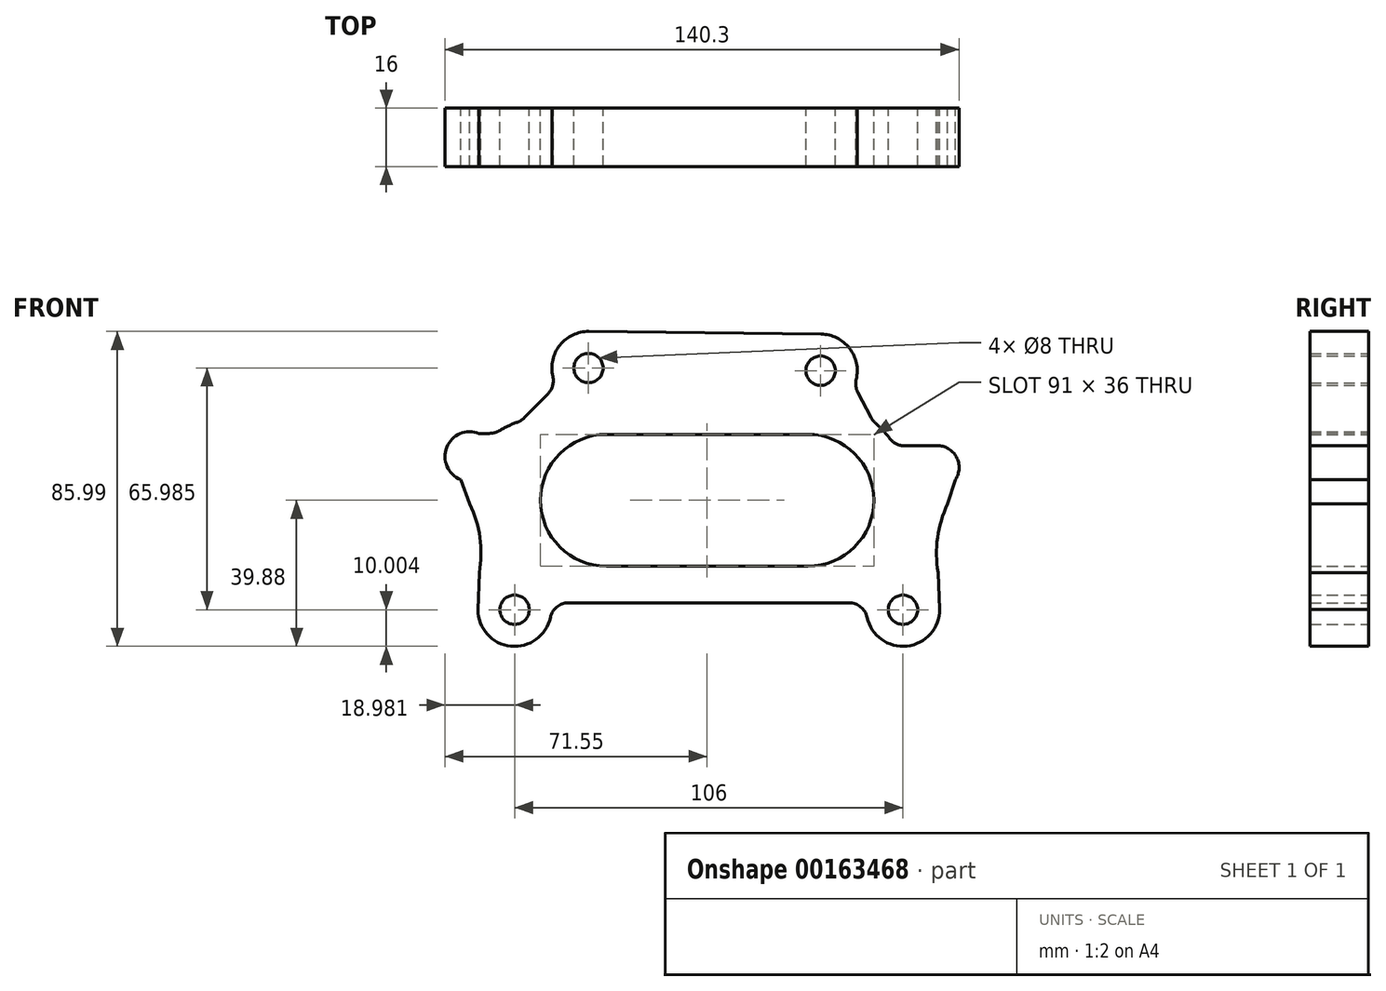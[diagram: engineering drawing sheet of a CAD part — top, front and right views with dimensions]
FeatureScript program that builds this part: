
annotation { "Feature Type Name" : "Feature", "Feature Type Description" : "" }
export const myFeature = defineFeature(function(context is Context, id is Id, definition is map)
    precondition{}
    {
        {
            var Q0;
            Q0=qCreatedBy(makeId("Front.planeOp"),FACE);
            var sketch = newSketch(context, id + "F0", { "sketchPlane" : qUnion([Q0])});
            skLineSegment(sketch, "E0", {"start": v(0, 0) * mm, "end": v(55, 0) * mm, "construction": true});
            skArc(sketch, "E1", {"start": v(0, 18) * mm, "mid": v(-18, 0) * mm, "end": v(0, -18) * mm});
            skArc(sketch, "E2", {"start": v(55, -18) * mm, "mid": v(73, 0) * mm, "end": v(55, 18) * mm});
            skLineSegment(sketch, "E3", {"start": v(0, 18) * mm, "end": v(55, 18) * mm});
            skLineSegment(sketch, "E4", {"start": v(0, -18) * mm, "end": v(55, -18) * mm});
            skLineSegment(sketch, "E5", {"start": v(0, 0) * mm, "end": v(0, -30) * mm, "construction": true});
            skLineSegment(sketch, "E6", {"start": v(0, 0) * mm, "end": v(-25.07, -29.88) * mm, "construction": true});
            skLineSegment(sketch, "E7", {"start": v(0, -30) * mm, "end": v(66, -30) * mm, "construction": true});
            skPoint(sketch, "E8", {"position": v(-25.07, -29.88) * mm});
            skArc(sketch, "E9", {"start": v(-35.04, -29.08) * mm, "mid": v(-26.51, -39.77) * mm, "end": v(-15.29, -31.96) * mm});
            skLineSegment(sketch, "E10", {"start": v(-25.07, -29.88) * mm, "end": v(58.46, 35.38) * mm, "construction": true});
            skPoint(sketch, "E11", {"position": v(58.46, 35.38) * mm});
            skArc(sketch, "E12", {"start": v(68.18, 33.04) * mm, "mid": v(66.35, 41.53) * mm, "end": v(58.57, 45.38) * mm});
            skLineSegment(sketch, "E13", {"start": v(-25.07, -29.88) * mm, "end": v(-4.9, 36.1) * mm, "construction": true});
            skPoint(sketch, "E14", {"position": v(-4.9, 36.1) * mm});
            skArc(sketch, "E15", {"start": v(-4.78, 46.1) * mm, "mid": v(-12.7, 42.36) * mm, "end": v(-14.63, 33.81) * mm});
            skLineSegment(sketch, "E16", {"start": v(-25.07, -29.88) * mm, "end": v(80.93, -29.88) * mm, "construction": true});
            skPoint(sketch, "E17", {"position": v(80.93, -29.88) * mm});
            skArc(sketch, "E18", {"start": v(71.15, -31.96) * mm, "mid": v(82.31, -39.78) * mm, "end": v(90.9, -29.2) * mm});
            skLineSegment(sketch, "E19", {"start": v(-25.07, -29.88) * mm, "end": v(-34.75, 8.94) * mm, "construction": true});
            skLineSegment(sketch, "E20", {"start": v(-34.75, 8.94) * mm, "end": v(90.25, 8.94) * mm, "construction": true});
            skArc(sketch, "E21", {"start": v(95.28, 5.66) * mm, "mid": v(95.52, 11.82) * mm, "end": v(90.2, 14.94) * mm});
            skLineSegment(sketch, "E22", {"start": v(-25.07, -29.88) * mm, "end": v(-65.21, -14.47) * mm, "construction": true});
            skArc(sketch, "E23", {"start": v(-34.67, -19.75) * mm, "mid": v(-34.51, -10.18) * mm, "end": v(-37.28, -1.01) * mm});
            skLineSegment(sketch, "E24", {"start": v(80.93, -29.88) * mm, "end": v(121.08, -14.47) * mm, "construction": true});
            skArc(sketch, "E25", {"start": v(93.15, -1.01) * mm, "mid": v(90.37, -10.18) * mm, "end": v(90.53, -19.75) * mm});
            skLineSegment(sketch, "E26", {"start": v(68.61, 29.55) * mm, "end": v(72.28, 22.53) * mm});
            skLineSegment(sketch, "E27", {"start": v(81.42, 14.85) * mm, "end": v(90.2, 14.94) * mm});
            skLineSegment(sketch, "E28", {"start": v(95.28, 5.66) * mm, "end": v(93.15, -1.01) * mm});
            skLineSegment(sketch, "E29", {"start": v(90.93, -29.74) * mm, "end": v(90.53, -19.75) * mm});
            skLineSegment(sketch, "E30", {"start": v(27.5, 18) * mm, "end": v(27.5, 28) * mm, "construction": true});
            skLineSegment(sketch, "E31", {"start": v(-34.75, 18.27) * mm, "end": v(-31.85, 18.27) * mm});
            skLineSegment(sketch, "E32", {"start": v(-15.92, 29.17) * mm, "end": v(-22.42, 22.53) * mm});
            skLineSegment(sketch, "E33", {"start": v(-39.77, 5.66) * mm, "end": v(-37.28, -1.01) * mm});
            skLineSegment(sketch, "E34", {"start": v(-34.67, -19.75) * mm, "end": v(-35.07, -29.88) * mm});
            skLineSegment(sketch, "E35", {"start": v(27.5, -18) * mm, "end": v(27.5, -28) * mm, "construction": true});
            skLineSegment(sketch, "E36", {"start": v(27.5, -28) * mm, "end": v(-10.4, -28) * mm});
            skLineSegment(sketch, "E37", {"start": v(27.5, -28) * mm, "end": v(66.26, -28) * mm});
            skArc(sketch, "E38.trimOffspring", {"start": v(-24.32, 21.31) * mm, "mid": v(-26.86, 20.27) * mm, "end": v(-29.28, 18.98) * mm});
            skArc(sketch, "E39.trimOffspring", {"start": v(-34.75, 18.27) * mm, "mid": v(-43.56, 14.47) * mm, "end": v(-39.77, 5.66) * mm});
            skArc(sketch, "E40.trimOffspring", {"start": v(77.37, 16.84) * mm, "mid": v(75.5, 19.06) * mm, "end": v(73.42, 21.08) * mm});
            skPoint(sketch, "E41.visualSharp", {"position": v(0.96, 28) * mm});
            skPoint(sketch, "E42.visualSharp", {"position": v(51.72, 28) * mm});
            skPoint(sketch, "E43.visualSharp", {"position": v(-15.25, -28) * mm});
            skArc(sketch, "E43.filletArc", {"start": v(-10.4, -28) * mm, "mid": v(-13.54, -29.11) * mm, "end": v(-15.29, -31.96) * mm});
            skPoint(sketch, "E44.visualSharp", {"position": v(71.1, -28) * mm});
            skArc(sketch, "E44.filletArc", {"start": v(71.15, -31.96) * mm, "mid": v(69.4, -29.11) * mm, "end": v(66.26, -28) * mm});
            skPoint(sketch, "E45.visualSharp", {"position": v(67.64, 31.41) * mm});
            skArc(sketch, "E45.filletArc", {"start": v(68.18, 33.04) * mm, "mid": v(68.08, 31.26) * mm, "end": v(68.61, 29.55) * mm});
            skPoint(sketch, "E46.visualSharp", {"position": v(72.74, 21.67) * mm});
            skArc(sketch, "E46.filletArc", {"start": v(72.28, 22.53) * mm, "mid": v(72.79, 21.76) * mm, "end": v(73.42, 21.08) * mm});
            skPoint(sketch, "E47.visualSharp", {"position": v(78.76, 14.82) * mm});
            skArc(sketch, "E47.filletArc", {"start": v(77.37, 16.84) * mm, "mid": v(79.16, 15.36) * mm, "end": v(81.42, 14.85) * mm});
            skPoint(sketch, "E48.visualSharp", {"position": v(-30.4, 18.27) * mm});
            skArc(sketch, "E48.filletArc", {"start": v(-31.85, 18.27) * mm, "mid": v(-30.52, 18.45) * mm, "end": v(-29.28, 18.98) * mm});
            skPoint(sketch, "E49.visualSharp", {"position": v(-23.26, 21.67) * mm});
            skArc(sketch, "E49.filletArc", {"start": v(-24.32, 21.31) * mm, "mid": v(-23.3, 21.81) * mm, "end": v(-22.42, 22.53) * mm});
            skPoint(sketch, "E50.visualSharp", {"position": v(-13.72, 31.41) * mm});
            skArc(sketch, "E50.filletArc", {"start": v(-15.92, 29.17) * mm, "mid": v(-14.68, 31.32) * mm, "end": v(-14.63, 33.81) * mm});
            skLineSegment(sketch, "E51", {"start": v(-4.78, 46.1) * mm, "end": v(58.85, 45.38) * mm});
            skPoint(sketch, "E51.startSnap0", {"position": v(-5, 46.1) * mm});
            skPoint(sketch, "E51.endSnap0", {"position": v(58.85, 45.38) * mm});
            skSolve(sketch);
        }
        {
            var Q0;
            Q0=makeQuery(id+"F0.imprint","IMPRINT",FACE,{"disambiguationData":[TD([[makeQuery(id+"F0.imprint","IMPRINT",EDGE,{"derivedFrom":sQuery(id+"F0.wireOp",EDGE,"E1")}),-1.0]])]});
            extrude(context, id + "F1", {"entities" : qUnion([Q0]), "depth" : 16 * mm});
        }
        {
            var Q0;
            Q0=sQuery(id+"F0.wireOp",VERTEX,"E11");
            var Q1;
            Q1=sQuery(id+"F0.wireOp",VERTEX,"E14");
            var Q2;
            Q2=sQuery(id+"F0.wireOp",VERTEX,"E8");
            var Q3;
            Q3=sQuery(id+"F0.wireOp",VERTEX,"E17");
            var Q4;
            Q4=makeQuery(id+"F1.opExtrude","SWEPT_BODY",BODY,{"disambiguationData":[OSD([sQuery(id+"F0.wireOp",EDGE,"E1"),sQuery(id+"F0.wireOp",EDGE,"E2"),sQuery(id+"F0.wireOp",EDGE,"E3"),sQuery(id+"F0.wireOp",EDGE,"E4"),sQuery(id+"F0.wireOp",EDGE,"E9"),sQuery(id+"F0.wireOp",EDGE,"E12"),sQuery(id+"F0.wireOp",EDGE,"E15"),sQuery(id+"F0.wireOp",EDGE,"E18"),sQuery(id+"F0.wireOp",EDGE,"E21"),sQuery(id+"F0.wireOp",EDGE,"E23"),sQuery(id+"F0.wireOp",EDGE,"E25"),sQuery(id+"F0.wireOp",EDGE,"E26"),sQuery(id+"F0.wireOp",EDGE,"E27"),sQuery(id+"F0.wireOp",EDGE,"E28"),sQuery(id+"F0.wireOp",EDGE,"E29"),sQuery(id+"F0.wireOp",EDGE,"n6l1QVvH-8axh-K2ot-TxVT-wgRIc5WpONdm"),sQuery(id+"F0.wireOp",EDGE,"KY1iZR6C-kT2c-u7T7-yr67-WwgEOI9Uij45"),sQuery(id+"F0.wireOp",EDGE,"E31"),sQuery(id+"F0.wireOp",EDGE,"E32"),sQuery(id+"F0.wireOp",EDGE,"E33"),sQuery(id+"F0.wireOp",EDGE,"E34"),sQuery(id+"F0.wireOp",EDGE,"E36"),sQuery(id+"F0.wireOp",EDGE,"E37"),sQuery(id+"F0.wireOp",EDGE,"E38.trimOffspring"),sQuery(id+"F0.wireOp",EDGE,"E39.trimOffspring"),sQuery(id+"F0.wireOp",EDGE,"E40.trimOffspring"),sQuery(id+"F0.wireOp",EDGE,"E41.filletArc"),sQuery(id+"F0.wireOp",EDGE,"E42.filletArc"),sQuery(id+"F0.wireOp",EDGE,"E43.filletArc"),sQuery(id+"F0.wireOp",EDGE,"E44.filletArc"),sQuery(id+"F0.wireOp",EDGE,"E45.filletArc"),sQuery(id+"F0.wireOp",EDGE,"E46.filletArc"),sQuery(id+"F0.wireOp",EDGE,"E47.filletArc"),sQuery(id+"F0.wireOp",EDGE,"E48.filletArc"),sQuery(id+"F0.wireOp",EDGE,"E49.filletArc"),sQuery(id+"F0.wireOp",EDGE,"E50.filletArc")])]});
            hole(context, id + "F2", {"style" : HoleStyle.SIMPLE, "endStyle" : HoleEndStyle.THROUGH, "oppositeDirection" : true, "holeDiameter" : 8 * mm, "locations" : qUnion([Q0, Q1, Q2, Q3]), "scope" : qUnion([Q4]), "isTappedThrough" : true});
        }
    });
